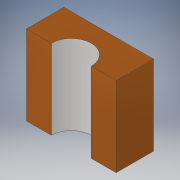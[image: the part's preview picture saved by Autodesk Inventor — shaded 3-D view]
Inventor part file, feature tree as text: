
AUTODESK INVENTOR PART (.ipt)
format: ipt  version: 2017 (Build 210142000, 142)  size: 106,496 bytes
history: native  units: mm
features: extrude x2, sketch x2, projected_geometry x1
ambient origin geometry x8: Origin, YZ Plane, XZ Plane, XY Plane, X Axis, Y Axis, Z Axis, Center Point
bodies: Solid1 (feature_tree)
feature tree (5):
  extrude  "Extrusion1"  Depth=16.0mm
  extrude  "Extrusion2"  Depth=7.5mm TaperAngle=0.0deg
  sketch  "Sketch1"  dims[d1=18.0mm d2=16.0mm]
  sketch  "Sketch2"  dims[d3=18.0mm d5=7.5mm d6=0.0mm d8=8.0mm d9=10.0mm d10=0.0mm]
  projected_geometry  "Projected Loop1"
